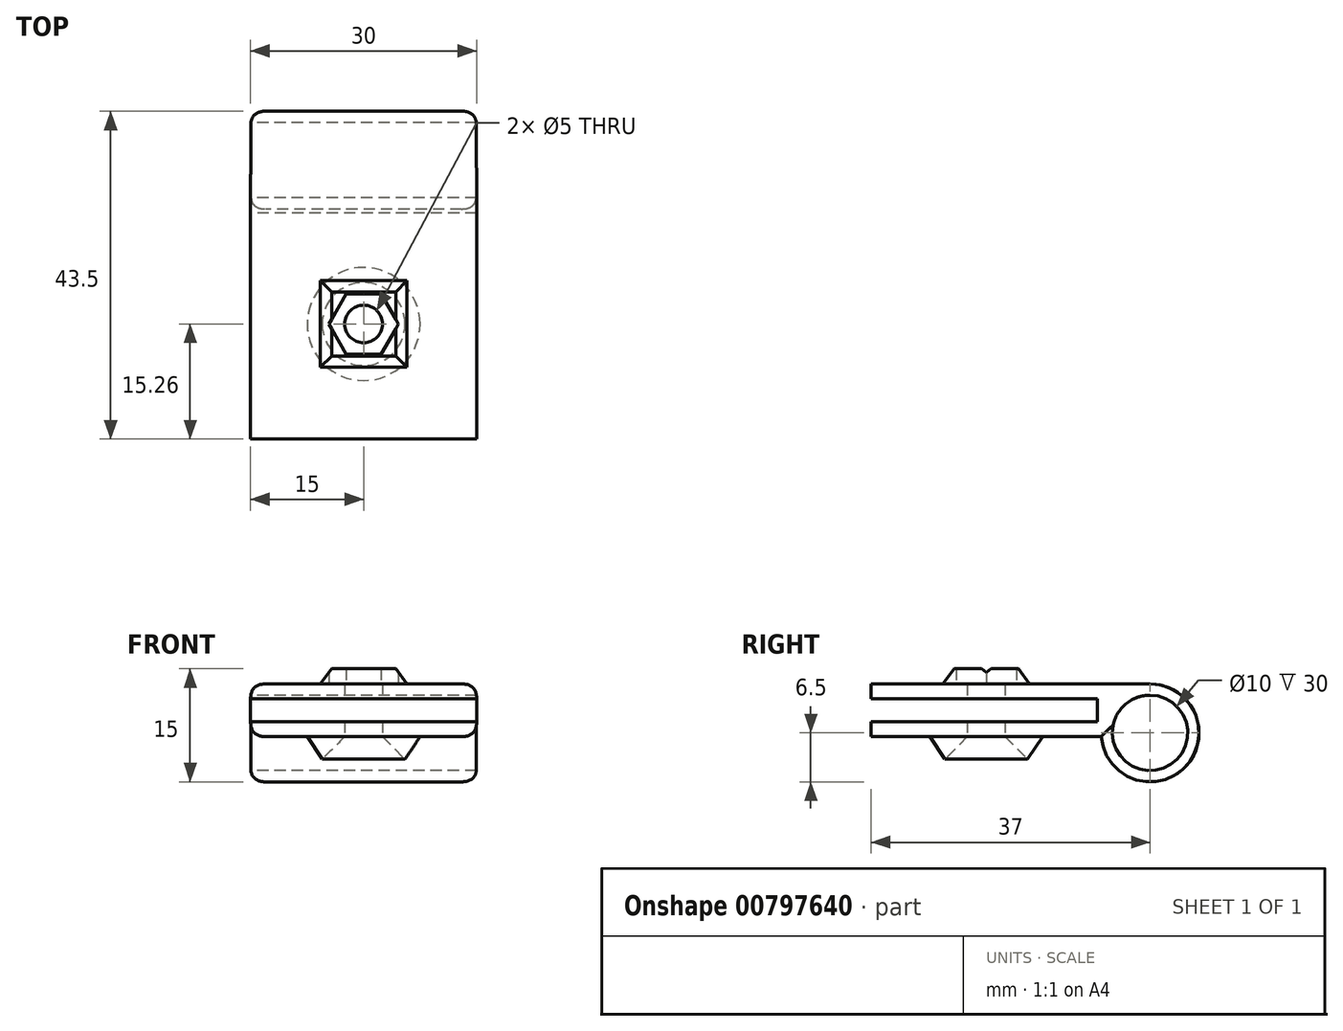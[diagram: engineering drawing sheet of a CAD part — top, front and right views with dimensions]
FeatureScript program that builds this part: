
annotation { "Feature Type Name" : "Feature", "Feature Type Description" : "" }
export const myFeature = defineFeature(function(context is Context, id is Id, definition is map)
    precondition{}
    {
        {
            var Q0;
            Q0=qCreatedBy(makeId("Right.planeOp"),FACE);
            var sketch = newSketch(context, id + "F0", { "sketchPlane" : qUnion([Q0])});
            skCircle(sketch, "E0", {"center": v(0, 0) * mm, "radius": 5 * mm});
            skCircle(sketch, "E1", {"center": v(0, 0) * mm, "radius": 6.5 * mm});
            skLineSegment(sketch, "E2", {"start": v(0, 6.5) * mm, "end": v(-37, 6.5) * mm});
            skLineSegment(sketch, "E3", {"start": v(-37, 6.5) * mm, "end": v(-37, 4.5) * mm});
            skLineSegment(sketch, "E4", {"start": v(-37, 4.5) * mm, "end": v(-7, 4.5) * mm});
            skLineSegment(sketch, "E5", {"start": v(-7, 4.5) * mm, "end": v(-7, 1.5) * mm});
            skLineSegment(sketch, "E6", {"start": v(-7, 1.5) * mm, "end": v(-37, 1.5) * mm});
            skLineSegment(sketch, "E7", {"start": v(-37, 1.5) * mm, "end": v(-37, -0.5) * mm});
            skLineSegment(sketch, "E8", {"start": v(-37, -0.5) * mm, "end": v(-6.48, -0.5) * mm});
            skSolve(sketch);
        }
        {
            var Q0;
            Q0 = qSketchRegion(id + "F0", true);
            extrude(context, id + "F1", {"entities" : qUnion([Q0]), "depth" : 30 * mm, "offsetDistance" : 25 * mm});
        }
        {
            var Q0;
            Q0=makeQuery(id+"F1.opExtrude","CAP_EDGE",EDGE,{"disambiguationData":[OSD([sQuery(id+"F0.wireOp",EDGE,"E8")])],"isStart":true});
            var Q1;
            Q1=makeQuery(id+"F1.opExtrude","CAP_EDGE",EDGE,{"disambiguationData":[OSD([sQuery(id+"F0.wireOp",EDGE,"E2")])],"isStart":true});
            var Q2;
            Q2=makeQuery(id+"F1.opExtrude","CAP_EDGE",EDGE,{"disambiguationData":[OSD([sQuery(id+"F0.wireOp",EDGE,"E8")])],"isStart":false});
            var Q3;
            Q3=makeQuery(id+"F1.opExtrude","CAP_EDGE",EDGE,{"disambiguationData":[OSD([sQuery(id+"F0.wireOp",EDGE,"E1")])],"isStart":false});
            fillet(context, id + "F2", {"entities" : qUnion([Q0, Q1, Q2, Q3]), "radius" : 2 * mm, "tangentPropagation" : true, "rho" : 0.5, "crossSection" : FilletCrossSection.CONIC, "allowEdgeOverflow" : false});
        }
        {
            var Q0;
            Q0=makeQuery(id+"F1.opExtrude","SWEPT_FACE",FACE,{"disambiguationData":[OSD([sQuery(id+"F0.wireOp",EDGE,"E8")])]});
            var sketch = newSketch(context, id + "F3", { "sketchPlane" : qUnion([Q0])});
            skLineSegment(sketch, "E9", {"start": v(28, 37) * mm, "end": v(28, 21.74) * mm});
            skPoint(sketch, "E10.endSnap0", {"position": v(15, 37) * mm});
            skCircle(sketch, "E11", {"center": v(15, 21.74) * mm, "radius": 2.5 * mm});
            skCircle(sketch, "E12", {"center": v(15, 21.74) * mm, "radius": 7.5 * mm});
            skSolve(sketch);
        }
        {
            var Q0;
            Q0=makeQuery(id+"F3.imprint","IMPRINT",FACE,{"disambiguationData":[TD([[makeQuery(id+"F3.imprint","IMPRINT",EDGE,{"derivedFrom":sQuery(id+"F3.wireOp",EDGE,"E11")}),1.0]])]});
            extrude(context, id + "F4", {"entities" : qUnion([Q0]), "operationType" : NewBodyOperationType.REMOVE, "oppositeDirection" : true, "depth" : 25 * mm, "offsetDistance" : 25 * mm});
        }
        {
            var Q0;
            Q0=makeQuery(id+"F3.imprint","IMPRINT",FACE,{"disambiguationData":[TD([[makeQuery(id+"F3.imprint","IMPRINT",EDGE,{"derivedFrom":sQuery(id+"F3.wireOp",EDGE,"E11")}),-1.0]])]});
            extrude(context, id + "F5", {"entities" : qUnion([Q0]), "operationType" : NewBodyOperationType.ADD, "depth" : 3 * mm, "offsetDistance" : 25 * mm});
        }
        {
            var Q0;
            Q0=makeQuery(id+"F5.opExtrude","CAP_EDGE",EDGE,{"disambiguationData":[OSD([sQuery(id+"F3.wireOp",EDGE,"E12")])],"isStart":false});
            chamfer(context, id + "F6", {"entities" : qUnion([Q0]), "chamferType" : ChamferType.TWO_OFFSETS, "width1" : 2 * mm, "oppositeDirection" : false, "width2" : 3 * mm, "tangentPropagation" : true});
        }
        {
            var Q0;
            Q0=makeQuery(id+"F5.opExtrude","CAP_EDGE",EDGE,{"disambiguationData":[OSD([sQuery(id+"F3.wireOp",EDGE,"E11")])],"isStart":false});
            chamfer(context, id + "F7", {"entities" : qUnion([Q0]), "width" : 3 * mm, "tangentPropagation" : true});
        }
        {
            var Q0;
            Q0=makeQuery(id+"F1.opExtrude","SWEPT_FACE",FACE,{"disambiguationData":[OSD([sQuery(id+"F0.wireOp",EDGE,"E2")])]});
            var sketch = newSketch(context, id + "F8", { "sketchPlane" : qUnion([Q0])});
            skCircle(sketch, "E13.cCircle", {"center": v(15, -21.74) * mm, "radius": 4 * mm, "construction": true});
            skLineSegment(sketch, "E13.0", {"start": v(17.3, -25.74) * mm, "end": v(12.7, -25.74) * mm});
            skLineSegment(sketch, "E13.1", {"start": v(12.7, -25.74) * mm, "end": v(10.38, -21.74) * mm});
            skLineSegment(sketch, "E13.2", {"start": v(10.38, -21.74) * mm, "end": v(12.7, -17.74) * mm});
            skLineSegment(sketch, "E13.3", {"start": v(12.7, -17.74) * mm, "end": v(17.3, -17.74) * mm});
            skLineSegment(sketch, "E13.4", {"start": v(17.3, -17.74) * mm, "end": v(19.62, -21.74) * mm});
            skLineSegment(sketch, "E13.5", {"start": v(19.62, -21.74) * mm, "end": v(17.3, -25.74) * mm});
            skPoint(sketch, "E13.0.midPoint", {"position": v(15, -25.74) * mm});
            skLineSegment(sketch, "E14.bottom", {"start": v(20.75, -16) * mm, "end": v(9.25, -16) * mm});
            skLineSegment(sketch, "E14.top", {"start": v(20.75, -27.5) * mm, "end": v(9.25, -27.5) * mm});
            skLineSegment(sketch, "E14.left", {"start": v(20.75, -16) * mm, "end": v(20.75, -27.5) * mm});
            skLineSegment(sketch, "E14.right", {"start": v(9.25, -16) * mm, "end": v(9.25, -27.5) * mm});
            skSolve(sketch);
        }
        {
            var Q0;
            Q0=makeQuery(id+"F8.imprint","IMPRINT",FACE,{"disambiguationData":[TD([[makeQuery(id+"F8.imprint","IMPRINT",EDGE,{"derivedFrom":sQuery(id+"F8.wireOp",EDGE,"E13.0")}),1.0]])]});
            extrude(context, id + "F9", {"entities" : qUnion([Q0]), "operationType" : NewBodyOperationType.ADD, "depth" : 2 * mm, "offsetDistance" : 25 * mm});
        }
        {
            var Q0;
            Q0=makeQuery(id+"F9.opExtrude","CAP_EDGE",EDGE,{"disambiguationData":[OSD([sQuery(id+"F8.wireOp",EDGE,"E14.left")])],"isStart":false});
            var Q1;
            Q1=makeQuery(id+"F9.opExtrude","CAP_EDGE",EDGE,{"disambiguationData":[OSD([sQuery(id+"F8.wireOp",EDGE,"E14.top")])],"isStart":false});
            var Q2;
            Q2=makeQuery(id+"F9.opExtrude","CAP_EDGE",EDGE,{"disambiguationData":[OSD([sQuery(id+"F8.wireOp",EDGE,"E14.right")])],"isStart":false});
            var Q3;
            Q3=makeQuery(id+"F9.opExtrude","CAP_EDGE",EDGE,{"disambiguationData":[OSD([sQuery(id+"F8.wireOp",EDGE,"E14.bottom")])],"isStart":false});
            chamfer(context, id + "F10", {"entities" : qUnion([Q0, Q1, Q2, Q3]), "chamferType" : ChamferType.TWO_OFFSETS, "width1" : 2 * mm, "oppositeDirection" : false, "width2" : 1.5 * mm, "tangentPropagation" : true});
        }
    });
